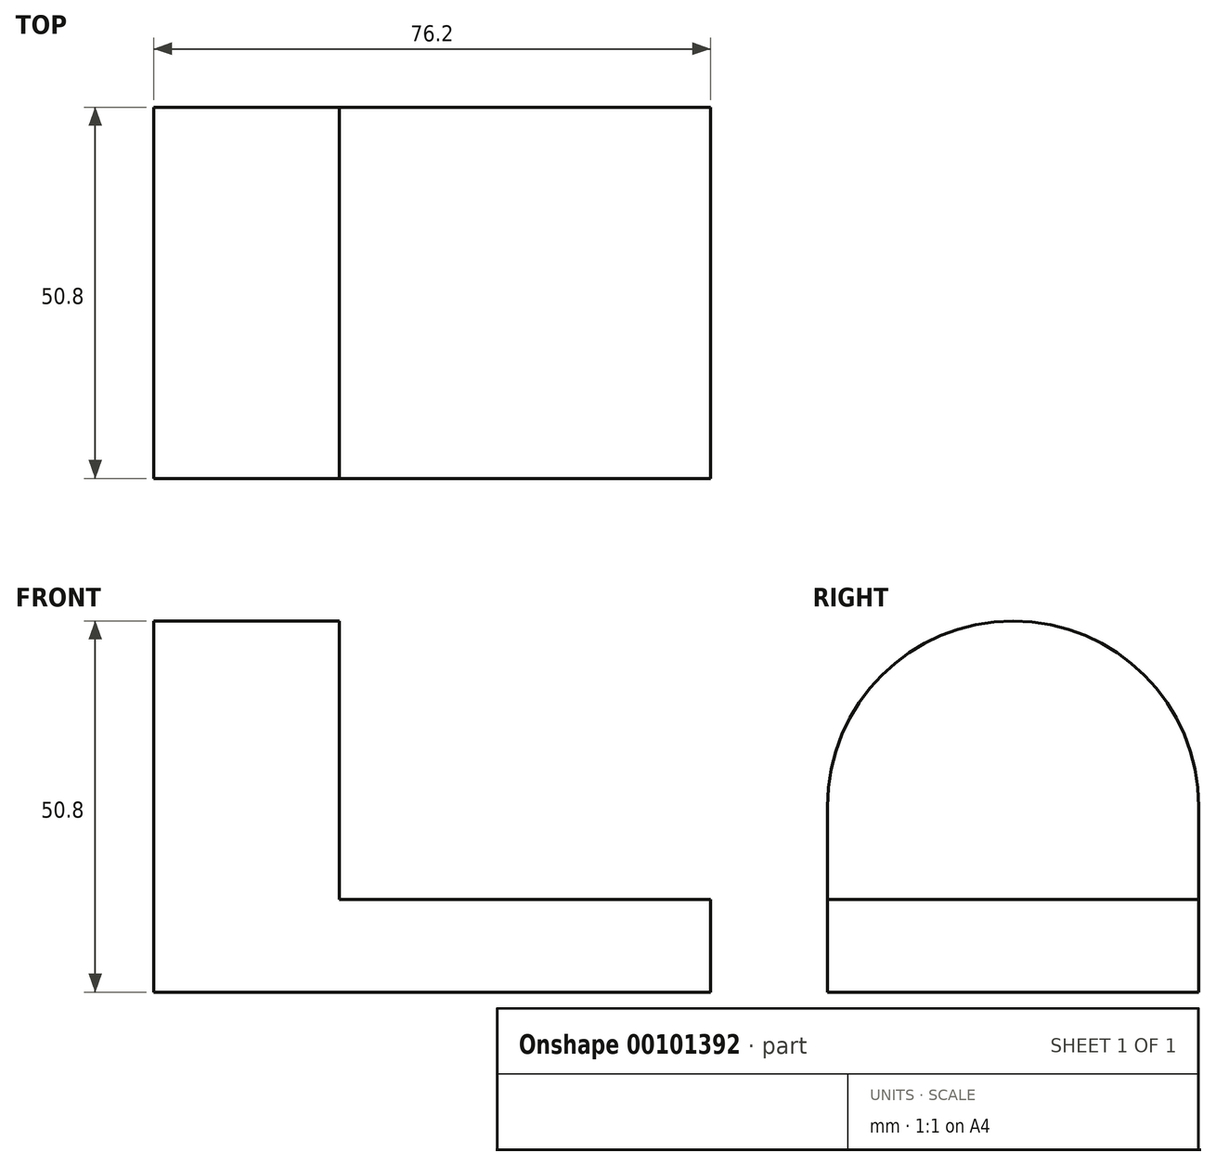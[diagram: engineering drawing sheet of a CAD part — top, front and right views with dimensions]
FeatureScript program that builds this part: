
annotation { "Feature Type Name" : "Feature", "Feature Type Description" : "" }
export const myFeature = defineFeature(function(context is Context, id is Id, definition is map)
    precondition{}
    {
        {
            var Q0;
            Q0=qCreatedBy(makeId("Front.planeOp"),FACE);
            var sketch = newSketch(context, id + "F0", { "sketchPlane" : qUnion([Q0])});
            skLineSegment(sketch, "E0", {"start": v(0, 0) * mm, "end": v(0, 50.8) * mm});
            skLineSegment(sketch, "E1", {"start": v(0, 50.8) * mm, "end": v(25.4, 50.8) * mm});
            skLineSegment(sketch, "E2", {"start": v(25.4, 50.8) * mm, "end": v(25.4, 12.7) * mm});
            skLineSegment(sketch, "E3", {"start": v(25.4, 12.7) * mm, "end": v(76.2, 12.7) * mm});
            skLineSegment(sketch, "E4", {"start": v(76.2, 12.7) * mm, "end": v(76.2, 0) * mm});
            skLineSegment(sketch, "E5", {"start": v(76.2, 0) * mm, "end": v(0, 0) * mm});
            skSolve(sketch);
        }
        {
            var Q0;
            Q0=qCreatedBy(makeId("Right.planeOp"),FACE);
            var sketch = newSketch(context, id + "F1", { "sketchPlane" : qUnion([Q0])});
            skLineSegment(sketch, "E6", {"start": v(25.4, 50.8) * mm, "end": v(25.4, 50.8) * mm});
            skPoint(sketch, "E7.visualSharp", {"position": v(0, 50.8) * mm});
            skArc(sketch, "E7.filletArc", {"start": v(25.4, 50.8) * mm, "mid": v(7.44, 43.36) * mm, "end": v(0, 25.4) * mm});
            skPoint(sketch, "E8.visualSharp", {"position": v(50.8, 50.8) * mm});
            skArc(sketch, "E8.filletArc", {"start": v(50.8, 25.4) * mm, "mid": v(43.36, 43.36) * mm, "end": v(25.4, 50.8) * mm});
            skLineSegment(sketch, "E9", {"start": v(50.8, 25.4) * mm, "end": v(50.8, 50.8) * mm});
            skLineSegment(sketch, "E10", {"start": v(50.8, 50.8) * mm, "end": v(25.4, 50.8) * mm});
            skLineSegment(sketch, "E11", {"start": v(0, 50.8) * mm, "end": v(0, 25.4) * mm});
            skLineSegment(sketch, "E12", {"start": v(0, 50.8) * mm, "end": v(25.4, 50.8) * mm});
            skLineSegment(sketch, "E13", {"start": v(0, 50.8) * mm, "end": v(0, 0) * mm});
            skLineSegment(sketch, "E14", {"start": v(50.8, 50.8) * mm, "end": v(50.8, 0) * mm});
            skSolve(sketch);
        }
        {
            var Q0;
            Q0=makeQuery(id+"F0.imprint","IMPRINT",FACE,{"disambiguationData":[TD([[makeQuery(id+"F0.imprint","IMPRINT",EDGE,{"derivedFrom":sQuery(id+"F0.wireOp",EDGE,"E0")}),-1.0]])]});
            extrude(context, id + "F2", {"entities" : qUnion([Q0]), "oppositeDirection" : true, "depth" : 50.8 * mm});
        }
        {
            var Q0;
            Q0 = qSketchRegion(id + "F1", true);
            extrude(context, id + "F3", {"entities" : qUnion([Q0]), "operationType" : NewBodyOperationType.REMOVE, "depth" : 25.4 * mm});
        }
    });
